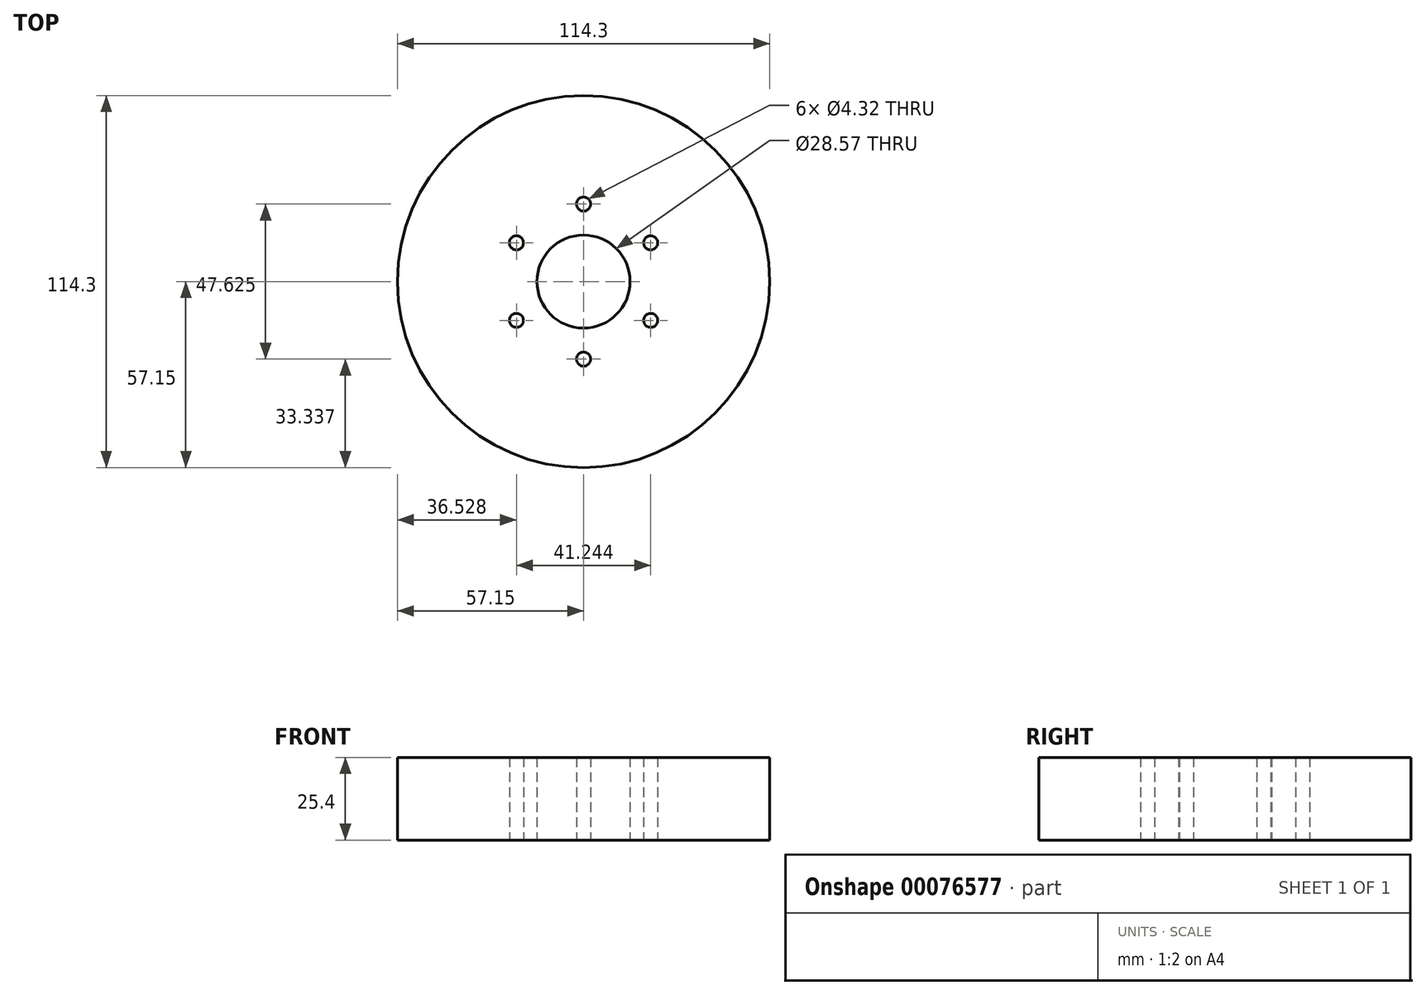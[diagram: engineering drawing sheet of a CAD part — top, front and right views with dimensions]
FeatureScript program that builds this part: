
annotation { "Feature Type Name" : "Feature", "Feature Type Description" : "" }
export const myFeature = defineFeature(function(context is Context, id is Id, definition is map)
    precondition{}
    {
        {
            var Q0;
            Q0=qCreatedBy(makeId("Top.planeOp"),FACE);
            var sketch = newSketch(context, id + "F0", { "sketchPlane" : qUnion([Q0])});
            skCircle(sketch, "E0", {"center": v(0, 0) * mm, "radius": 57.15 * mm});
            skCircle(sketch, "E1", {"center": v(0, 0) * mm, "radius": 14.29 * mm});
            skCircle(sketch, "E2.cCircle", {"center": v(0, 0) * mm, "radius": 23.81 * mm, "construction": true});
            skLineSegment(sketch, "E2.0", {"start": v(0, 23.81) * mm, "end": v(20.62, 11.9) * mm, "construction": true});
            skLineSegment(sketch, "E2.1", {"start": v(20.62, 11.9) * mm, "end": v(20.62, -11.9) * mm, "construction": true});
            skLineSegment(sketch, "E2.2", {"start": v(20.62, -11.9) * mm, "end": v(0, -23.81) * mm, "construction": true});
            skLineSegment(sketch, "E2.3", {"start": v(0, -23.81) * mm, "end": v(-20.62, -11.9) * mm, "construction": true});
            skLineSegment(sketch, "E2.4", {"start": v(-20.62, -11.9) * mm, "end": v(-20.62, 11.9) * mm, "construction": true});
            skLineSegment(sketch, "E2.5", {"start": v(-20.62, 11.9) * mm, "end": v(0, 23.81) * mm, "construction": true});
            skCircle(sketch, "E3", {"center": v(0, 23.81) * mm, "radius": 2.16 * mm});
            skCircle(sketch, "E4", {"center": v(20.62, 11.9) * mm, "radius": 2.16 * mm});
            skCircle(sketch, "E5", {"center": v(20.62, -11.9) * mm, "radius": 2.16 * mm});
            skCircle(sketch, "E6", {"center": v(0, -23.81) * mm, "radius": 2.16 * mm});
            skCircle(sketch, "E7", {"center": v(-20.62, -11.9) * mm, "radius": 2.16 * mm});
            skCircle(sketch, "E8", {"center": v(-20.62, 11.9) * mm, "radius": 2.16 * mm});
            skSolve(sketch);
        }
        {
            var Q0;
            Q0=makeQuery(id+"F0.imprint","IMPRINT",FACE,{"disambiguationData":[TD([[makeQuery(id+"F0.imprint","IMPRINT",EDGE,{"derivedFrom":sQuery(id+"F0.wireOp",EDGE,"E0")}),1.0]])]});
            extrude(context, id + "F1", {"entities" : qUnion([Q0]), "depth" : 25.4 * mm});
        }
    });
